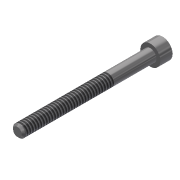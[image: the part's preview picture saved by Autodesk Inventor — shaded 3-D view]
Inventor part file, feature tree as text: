
AUTODESK INVENTOR PART (.ipt)
format: ipt  version: 2013 (Build 170138000, 138)  size: 94,208 bytes
history: native  units: in
note: dims shown in document units (in); Inventor stores cm internally (conversion verified against a paired STEP export)
features: extrude x3, sketch x3, chamfer x1, thread x1
ambient origin geometry x8: Origin, YZ Plane, XZ Plane, XY Plane, X Axis, Y Axis, Z Axis, Center Point
bodies: Solid1 (feature_tree)
feature tree (8):
  extrude  "Extrusion1"  Depth=1.5in TaperAngle=0.0deg
  extrude  "Extrusion2"  Depth=0.138in TaperAngle=0.0deg
  extrude  "Extrusion3"  Depth=0.069in TaperAngle=0.0deg
  chamfer  "Chamfer1"  Distance=0.02in Angle=45.0deg
  thread  "Thread2"  [1 undecoded]
  sketch  "Sketch1"  dims[d0=0.138in d1=1.5in d2=0.0in]
  sketch  "Sketch2"  dims[d3=0.226in d4=0.138in d5=0.0in]
  sketch  "Sketch3"  dims[d6=0.1094in d7=0.069in d8=0.0in d11=0.02in d12=0.125in d13=45.0deg d14=1.0in d15=0.0in]
note: 1 required parameter value undecoded (feature->parameter linkage not recoverable at this tier; creation-order binding heuristic only, values carry confidence <= 0.55)
